# Revit family: Artek_Shelving_Kaari Wall Shelf_Kaari REB006
name_source: partatom
category: Furniture
revit_build: Autodesk Revit 2017 (Build: 20190508_0315(x64)
units: mm (PartAtom-declared; Revit-internal decimal feet)

## family parameters
Cut with Voids When Loaded = No
Host = Face
OmniClass Number = 23.40.20.27
OmniClass Title = Storage Shelving
Room Calculation Point = No
Shared = No

## types (3) — shared parameters
AssetType = Movable
BIMObjectName = Artek_Shelving_Kaari Wall Console _Kaari REB006
Brand = Artek
Category = Shelving
Collection = Kaari Collection
Color = Black/red/blue
ConvergoRefNr = 0190-2009-0039-FI
Designer = Ronan & Erwan Bouroullec
DurationUnit = Years
IfcExportAs = IfcFurnitureType
IfcExportType = SHELF
MainColor = Black/red/blue
Manufacturer = Artek
ManufacturerName = Artek
ManufacturerURL = https://www.artek.fi
Material = Wood/Steel
Model = Kaari Wall Console REB006 - Red shelf, black edge
ModelNumber = 28503102
NBSDescription = Shelf units
NBSReference = 45-35-80/310
Name = Kaari REB006
NominalDepth = 341 mm
NominalHeight = 1000 mm  [stored 3.28084 ft]
NominalWidth = 450 mm
Shape = Sculptured
Size = 1000x350x450 mm
URL = https://www.artek.fi
Uniclass2 = Pr_40_30_78_77
Uniclass2015Description = Shelf units
Uniclass2015Reference = Pr_40_30_78_77
Version = 1
VersionDate = 11/3/2020
WarrantyDurationUnit = Years
zero-valued in all types: Default Elevation

## per-type parameters (varying)
| type | ShelfEdgeMaterial | ShelfMaterial |
| Kaari Wall Console REB006 - Red shelf, black edge | Linoleum black | Linoleum red |
| Kaari Wall Console REB006 - Blue shelf, red edge | Linoleum red | Linoleum blue |
| Kaari Wall Console REB006 - Black shelf, black edge | Linoleum black | Linoleum black |

note: [stored X ft] marks values corroborated as IEEE doubles in the binary element streams (Revit-internal decimal feet)

## geometry (parser evidence)
native form markers: Sweep x6
no freeform markers — native parametric forms only
